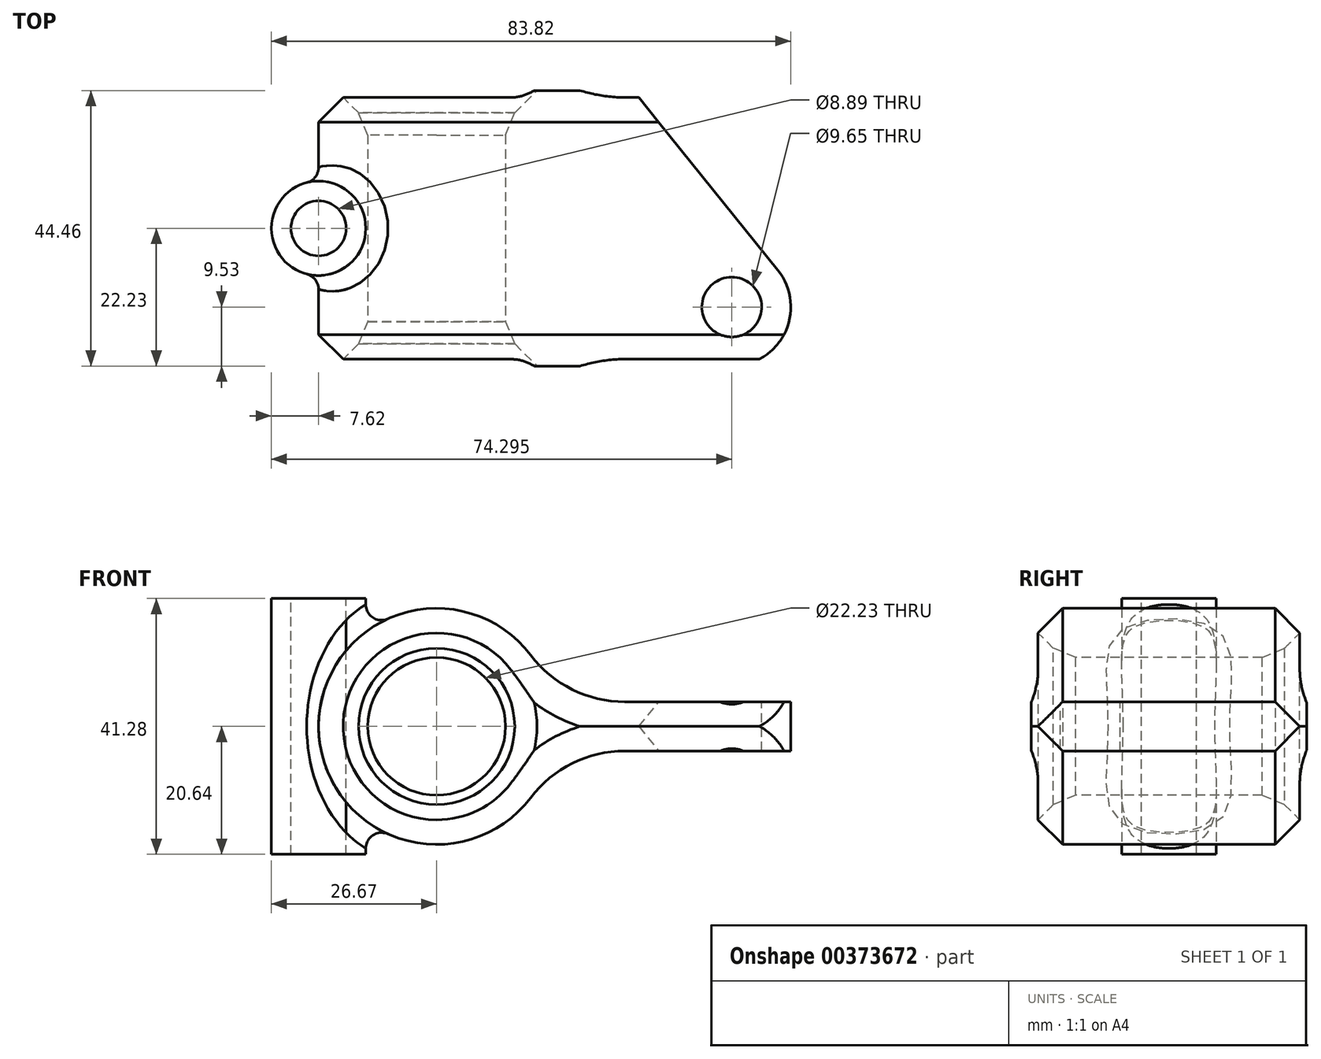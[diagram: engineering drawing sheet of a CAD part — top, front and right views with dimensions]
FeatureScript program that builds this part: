
annotation { "Feature Type Name" : "Feature", "Feature Type Description" : "" }
export const myFeature = defineFeature(function(context is Context, id is Id, definition is map)
    precondition{}
    {
        {
            var Q0;
            Q0=qCreatedBy(makeId("Front.planeOp"),FACE);
            var sketch = newSketch(context, id + "F0", { "sketchPlane" : qUnion([Q0])});
            skCircle(sketch, "E0", {"center": v(0, 0) * mm, "radius": 19.05 * mm});
            skSolve(sketch);
        }
        {
            var Q0;
            Q0=makeQuery(id+"F0.imprint","IMPRINT",FACE,{"disambiguationData":[TD([[makeQuery(id+"F0.imprint","IMPRINT",EDGE,{"derivedFrom":sQuery(id+"F0.wireOp",EDGE,"E0")}),1.0]])]});
            extrude(context, id + "F1", {"entities" : qUnion([Q0]), "depth" : 44.45 * mm, "symmetric" : true});
        }
        {
            var Q0;
            Q0=qCreatedBy(makeId("Top.planeOp"),FACE);
            var sketch = newSketch(context, id + "F2", { "sketchPlane" : qUnion([Q0])});
            skLineSegment(sketch, "E1.0", {"start": v(19.05, -22.23) * mm, "end": v(-19.05, -22.23) * mm});
            skLineSegment(sketch, "E1.1", {"start": v(19.05, 22.23) * mm, "end": v(-19.05, 22.23) * mm});
            skCircle(sketch, "E2", {"center": v(-19.05, 0) * mm, "radius": 7.62 * mm});
            skSolve(sketch);
        }
        {
            var Q0;
            Q0=makeQuery(id+"F2.imprint","IMPRINT",FACE,{"disambiguationData":[TD([[makeQuery(id+"F2.imprint","IMPRINT",EDGE,{"derivedFrom":sQuery(id+"F2.wireOp",EDGE,"E2")}),1.0]])]});
            extrude(context, id + "F3", {"entities" : qUnion([Q0]), "operationType" : NewBodyOperationType.ADD, "depth" : 41.27 * mm, "symmetric" : true});
        }
        {
            var Q0;
            Q0=qCreatedBy(makeId("Top.planeOp"),FACE);
            var sketch = newSketch(context, id + "F4", { "sketchPlane" : qUnion([Q0])});
            skLineSegment(sketch, "E3.0", {"start": v(19.05, 22.23) * mm, "end": v(-19.05, 22.23) * mm});
            skLineSegment(sketch, "E3.1", {"start": v(19.05, -22.23) * mm, "end": v(-19.05, -22.23) * mm});
            skLineSegment(sketch, "E4", {"start": v(0, -22.23) * mm, "end": v(0, 22.23) * mm});
            skLineSegment(sketch, "E5", {"start": v(0, 22.23) * mm, "end": v(31.75, 22.23) * mm});
            skLineSegment(sketch, "E6", {"start": v(31.75, 22.23) * mm, "end": v(55.05, -6.73) * mm});
            skLineSegment(sketch, "E7", {"start": v(19.05, -22.23) * mm, "end": v(47.63, -22.23) * mm});
            skArc(sketch, "E8", {"start": v(47.63, -22.23) * mm, "mid": v(56.22, -16.81) * mm, "end": v(55.05, -6.73) * mm});
            skSolve(sketch);
        }
        {
            var Q0;
            {var subQ3=sQuery(id+"F4.wireOp",EDGE,"E4");Q0=makeQuery(id+"F4.imprint","IMPRINT",FACE,{"disambiguationData":[TD([[makeQuery(id+"F4.imprint","IMPRINT",EDGE,{"derivedFrom":subQ3}),-1.0]])]});}
            extrude(context, id + "F5", {"entities" : qUnion([Q0]), "operationType" : NewBodyOperationType.ADD, "depth" : 7.94 * mm, "symmetric" : true});
        }
        {
            var Q0;
            Q0=makeQuery(id+"F3.opExtrude","CAP_FACE",FACE,{"disambiguationData":[OSD([sQuery(id+"F2.wireOp",EDGE,"E2")])],"isStart":false});
            var sketch = newSketch(context, id + "F6", { "sketchPlane" : qUnion([Q0])});
            skCircle(sketch, "E9.0", {"center": v(-19.05, 0) * mm, "radius": 4.44 * mm});
            skSolve(sketch);
        }
        {
            var Q0;
            Q0=makeQuery(id+"F6.imprint","IMPRINT",FACE,{"disambiguationData":[TD([[makeQuery(id+"F6.imprint","IMPRINT",EDGE,{"derivedFrom":sQuery(id+"F6.wireOp",EDGE,"E9.0")}),1.0]])]});
            extrude(context, id + "F7", {"entities" : qUnion([Q0]), "operationType" : NewBodyOperationType.REMOVE, "endBound" : BoundingType.THROUGH_ALL, "oppositeDirection" : true, "depth" : 25.4 * mm});
        }
        {
            var Q0;
            Q0=makeQuery(id+"F5.boolean.opBoolean","MERGE",FACE,{"derivedFrom":[makeQuery(id+"F1.opExtrude","CAP_FACE",FACE,{"disambiguationData":[OSD([sQuery(id+"F0.wireOp",EDGE,"E0")])],"isStart":false}),makeQuery(id+"F5.opExtrude","SWEPT_FACE",FACE,{"disambiguationData":[OSD([sQuery(id+"F4.wireOp",EDGE,"E3.1")])]})]});
            var sketch = newSketch(context, id + "F8", { "sketchPlane" : qUnion([Q0])});
            skCircle(sketch, "E10", {"center": v(0, 0) * mm, "radius": 11.11 * mm});
            skSolve(sketch);
        }
        {
            var Q0;
            Q0=makeQuery(id+"F8.imprint","IMPRINT",FACE,{"disambiguationData":[TD([[makeQuery(id+"F8.imprint","IMPRINT",EDGE,{"derivedFrom":sQuery(id+"F8.wireOp",EDGE,"E10")}),1.0]])]});
            extrude(context, id + "F9", {"entities" : qUnion([Q0]), "operationType" : NewBodyOperationType.REMOVE, "endBound" : BoundingType.THROUGH_ALL, "oppositeDirection" : true, "depth" : 25.4 * mm});
        }
        {
            var Q0;
            Q0=makeQuery(id+"F5.opExtrude","CAP_FACE",FACE,{"disambiguationData":[OSD([sQuery(id+"F4.wireOp",EDGE,"E3.1"),sQuery(id+"F4.wireOp",EDGE,"E4"),sQuery(id+"F4.wireOp",EDGE,"E5"),sQuery(id+"F4.wireOp",EDGE,"E6"),sQuery(id+"F4.wireOp",EDGE,"E8")])],"isStart":false});
            var sketch = newSketch(context, id + "F10", { "sketchPlane" : qUnion([Q0])});
            skCircle(sketch, "E11", {"center": v(47.63, -12.7) * mm, "radius": 4.83 * mm});
            skSolve(sketch);
        }
        {
            var Q0;
            Q0=makeQuery(id+"F10.imprint","IMPRINT",FACE,{"disambiguationData":[TD([[makeQuery(id+"F10.imprint","IMPRINT",EDGE,{"derivedFrom":sQuery(id+"F10.wireOp",EDGE,"E11")}),1.0]])]});
            extrude(context, id + "F11", {"entities" : qUnion([Q0]), "operationType" : NewBodyOperationType.ADD, "depth" : 25.4 * mm});
        }
        {
            var Q0;
            Q0=makeQuery(id+"F11.opExtrude","CAP_FACE",FACE,{"disambiguationData":[OSD([sQuery(id+"F10.wireOp",EDGE,"E11")])],"isStart":false});
            extrude(context, id + "F12", {"entities" : qUnion([Q0]), "operationType" : NewBodyOperationType.REMOVE, "endBound" : BoundingType.THROUGH_ALL, "oppositeDirection" : true, "depth" : 25.4 * mm});
        }
        {
            var Q0;
            Q0=makeQuery(id+"F5.boolean.opBoolean","INTERSECT",EDGE,{"derivedFrom":[makeQuery(id+"F1.opExtrude","SWEPT_FACE",FACE,{"disambiguationData":[OSD([sQuery(id+"F0.wireOp",EDGE,"E0")])]}),makeQuery(id+"F5.opExtrude","CAP_FACE",FACE,{"disambiguationData":[OSD([sQuery(id+"F4.wireOp",EDGE,"E3.1"),sQuery(id+"F4.wireOp",EDGE,"E4"),sQuery(id+"F4.wireOp",EDGE,"E5"),sQuery(id+"F4.wireOp",EDGE,"E6"),sQuery(id+"F4.wireOp",EDGE,"E8")])],"isStart":false})]});
            var Q1;
            Q1=makeQuery(id+"F5.boolean.opBoolean","INTERSECT",EDGE,{"derivedFrom":[makeQuery(id+"F1.opExtrude","SWEPT_FACE",FACE,{"disambiguationData":[OSD([sQuery(id+"F0.wireOp",EDGE,"E0")])]}),makeQuery(id+"F5.opExtrude","CAP_FACE",FACE,{"disambiguationData":[OSD([sQuery(id+"F4.wireOp",EDGE,"E3.1"),sQuery(id+"F4.wireOp",EDGE,"E4"),sQuery(id+"F4.wireOp",EDGE,"E5"),sQuery(id+"F4.wireOp",EDGE,"E6"),sQuery(id+"F4.wireOp",EDGE,"E8")])],"isStart":true})]});
            fillet(context, id + "F13", {"entities" : qUnion([Q0, Q1]), "radius" : 19.05 * mm, "tangentPropagation" : true, "allowEdgeOverflow" : false});
        }
        {
            var Q0;
            Q0=makeQuery(id+"F5.opExtrude","SWEPT_EDGE",EDGE,{"disambiguationData":[OSD([sQuery(id+"F4.wireOp",EDGE,"E5"),sQuery(id+"F4.wireOp",EDGE,"E6")])]});
            var Q1;
            Q1=makeQuery(id+"F3.boolean.opBoolean","INTERSECT",EDGE,{"derivedFrom":[makeQuery(id+"F1.opExtrude","SWEPT_FACE",FACE,{"disambiguationData":[OSD([sQuery(id+"F0.wireOp",EDGE,"E0")])]}),makeQuery(id+"F3.opExtrude","SWEPT_FACE",FACE,{"disambiguationData":[OSD([sQuery(id+"F2.wireOp",EDGE,"E2")])]})]});
            fillet(context, id + "F14", {"entities" : qUnion([Q0, Q1]), "radius" : 2.54 * mm, "tangentPropagation" : true, "allowEdgeOverflow" : false});
        }
        {
            var Q0;
            Q0=makeQuery(id+"F5.boolean.opBoolean","MERGE",FACE,{"derivedFrom":[makeQuery(id+"F1.opExtrude","CAP_FACE",FACE,{"disambiguationData":[OSD([sQuery(id+"F0.wireOp",EDGE,"E0")])],"isStart":false}),makeQuery(id+"F5.opExtrude","SWEPT_FACE",FACE,{"disambiguationData":[OSD([sQuery(id+"F4.wireOp",EDGE,"E3.1")])]})]});
            chamfer(context, id + "F15", {"entities" : qUnion([Q0]), "width" : 5.08 * mm});
        }
        {
            var Q0;
            Q0=makeQuery(id+"F5.boolean.opBoolean","MERGE",FACE,{"derivedFrom":[makeQuery(id+"F1.opExtrude","CAP_FACE",FACE,{"disambiguationData":[OSD([sQuery(id+"F0.wireOp",EDGE,"E0")])],"isStart":true}),makeQuery(id+"F5.opExtrude","SWEPT_FACE",FACE,{"disambiguationData":[OSD([sQuery(id+"F4.wireOp",EDGE,"E5")])]})]});
            chamfer(context, id + "F16", {"entities" : qUnion([Q0]), "width" : 5.08 * mm});
        }
        {
            var Q0;
            Q0=makeQuery(id+"F9.boolean.opBoolean","COPY",FACE,{"derivedFrom":makeQuery(id+"F9.opExtrude","SWEPT_FACE",FACE,{"disambiguationData":[OSD([sQuery(id+"F8.wireOp",EDGE,"E10")])]})});
            chamfer(context, id + "F17", {"entities" : qUnion([Q0]), "width" : 5.08 * mm, "tangentPropagation" : true});
        }
    });
